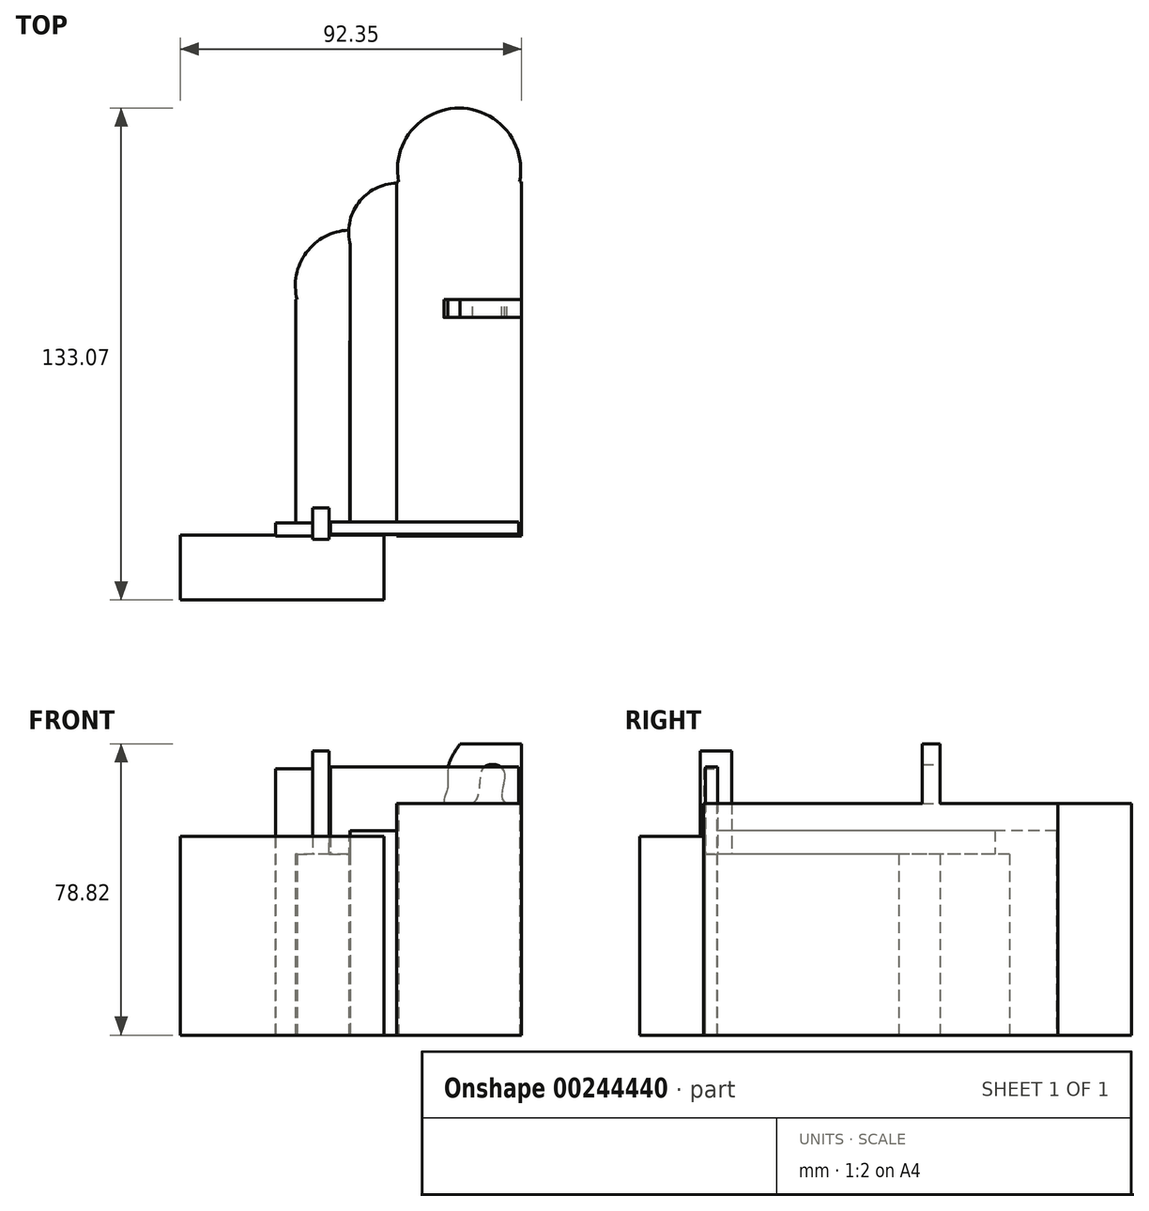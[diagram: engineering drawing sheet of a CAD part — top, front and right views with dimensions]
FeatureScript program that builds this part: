
annotation { "Feature Type Name" : "Feature", "Feature Type Description" : "" }
export const myFeature = defineFeature(function(context is Context, id is Id, definition is map)
    precondition{}
    {
        {
            var Q0;
            Q0=qCreatedBy(makeId("Top.planeOp"),FACE);
            var sketch = newSketch(context, id + "F0", { "sketchPlane" : qUnion([Q0])});
            skCircle(sketch, "E0", {"center": v(9.04, 35.12) * mm, "radius": 16.7 * mm});
            skSolve(sketch);
        }
        {
            var Q0;
            Q0 = qSketchRegion(id + "F0", true);
            extrude(context, id + "F1", {"entities" : qUnion([Q0]), "depth" : 62.74 * mm});
        }
        {
            var Q0;
            Q0=qCreatedBy(makeId("Top.planeOp"),FACE);
            var sketch = newSketch(context, id + "F2", { "sketchPlane" : qUnion([Q0])});
            skLineSegment(sketch, "E1.bottom", {"start": v(25.94, 31.92) * mm, "end": v(-7.87, 31.92) * mm});
            skLineSegment(sketch, "E1.top", {"start": v(25.94, -63.98) * mm, "end": v(-7.87, -63.98) * mm});
            skLineSegment(sketch, "E1.left", {"start": v(25.94, 31.92) * mm, "end": v(25.94, -63.98) * mm});
            skLineSegment(sketch, "E1.right", {"start": v(-7.87, 31.92) * mm, "end": v(-7.87, -63.98) * mm});
            skSolve(sketch);
        }
        {
            var Q0;
            Q0 = qSketchRegion(id + "F2", true);
            extrude(context, id + "F3", {"entities" : qUnion([Q0]), "operationType" : NewBodyOperationType.ADD, "depth" : 62.74 * mm});
        }
        {
            var Q0;
            Q0=qCreatedBy(makeId("Top.planeOp"),FACE);
            var sketch = newSketch(context, id + "F4", { "sketchPlane" : qUnion([Q0])});
            skCircle(sketch, "E2", {"center": v(-7.58, 18.24) * mm, "radius": 13.27 * mm});
            skSolve(sketch);
        }
        {
            var Q0;
            Q0 = qSketchRegion(id + "F4", true);
            extrude(context, id + "F5", {"entities" : qUnion([Q0]), "operationType" : NewBodyOperationType.ADD, "depth" : 55.37 * mm});
        }
        {
            var Q0;
            Q0=qCreatedBy(makeId("Top.planeOp"),FACE);
            var sketch = newSketch(context, id + "F6", { "sketchPlane" : qUnion([Q0])});
            skLineSegment(sketch, "E3.bottom", {"start": v(-7.87, 19.11) * mm, "end": v(-20.4, 19.11) * mm});
            skLineSegment(sketch, "E3.top", {"start": v(-7.87, -63.67) * mm, "end": v(-20.4, -63.67) * mm});
            skLineSegment(sketch, "E3.left", {"start": v(-7.87, 19.11) * mm, "end": v(-7.87, -63.67) * mm});
            skLineSegment(sketch, "E3.right", {"start": v(-20.4, 19.11) * mm, "end": v(-20.4, -63.67) * mm});
            skSolve(sketch);
        }
        {
            var Q0;
            Q0 = qSketchRegion(id + "F6", true);
            extrude(context, id + "F7", {"entities" : qUnion([Q0]), "operationType" : NewBodyOperationType.ADD, "depth" : 55.37 * mm});
        }
        {
            var Q0;
            Q0=qCreatedBy(makeId("Top.planeOp"),FACE);
            var sketch = newSketch(context, id + "F8", { "sketchPlane" : qUnion([Q0])});
            skCircle(sketch, "E4", {"center": v(-20.28, 3.79) * mm, "radius": 15 * mm});
            skSolve(sketch);
        }
        {
            var Q0;
            Q0 = qSketchRegion(id + "F8", true);
            extrude(context, id + "F9", {"entities" : qUnion([Q0]), "operationType" : NewBodyOperationType.ADD, "depth" : 49.02 * mm});
        }
        {
            var Q0;
            Q0=qCreatedBy(makeId("Top.planeOp"),FACE);
            var sketch = newSketch(context, id + "F10", { "sketchPlane" : qUnion([Q0])});
            skLineSegment(sketch, "E5.bottom", {"start": v(-20.57, 0) * mm, "end": v(-35.14, 0) * mm});
            skLineSegment(sketch, "E5.top", {"start": v(-20.57, -64.12) * mm, "end": v(-35.14, -64.12) * mm});
            skLineSegment(sketch, "E5.left", {"start": v(-20.57, 0) * mm, "end": v(-20.57, -64.12) * mm});
            skLineSegment(sketch, "E5.right", {"start": v(-35.14, 0) * mm, "end": v(-35.14, -64.12) * mm});
            skSolve(sketch);
        }
        {
            var Q0;
            Q0 = qSketchRegion(id + "F10", true);
            extrude(context, id + "F11", {"entities" : qUnion([Q0]), "operationType" : NewBodyOperationType.ADD, "depth" : 49.02 * mm});
        }
        {
            var Q0;
            Q0=qCreatedBy(makeId("Front.planeOp"),FACE);
            var sketch = newSketch(context, id + "F12", { "sketchPlane" : qUnion([Q0])});
            skLineSegment(sketch, "E6", {"start": v(25.94, 62.2) * mm, "end": v(25.94, 78.82) * mm});
            skLineSegment(sketch, "E7", {"start": v(25.94, 78.82) * mm, "end": v(9.33, 78.82) * mm});
            skFitSpline(sketch, "E8", {"points": [v(9.33, 78.82) * mm, v(6.12, 72.7) * mm, v(5.83, 66.58) * mm, v(5.25, 62.5) * mm, v(13.4, 63.38) * mm, v(15.74, 72.41) * mm, v(20.99, 71.83) * mm, v(20.7, 63.96) * mm, v(25.94, 62.2) * mm], "startDerivative": vector(-32.98, -46.7) * mm, "endDerivative": vector(61.94, -2.33) * mm});
            skSolve(sketch);
        }
        {
            var Q0;
            Q0 = qSketchRegion(id + "F12", true);
            extrude(context, id + "F13", {"entities" : qUnion([Q0]), "operationType" : NewBodyOperationType.ADD, "depth" : 4.83 * mm});
        }
        {
            var Q0;
            Q0=qCreatedBy(makeId("Top.planeOp"),FACE);
            var sketch = newSketch(context, id + "F14", { "sketchPlane" : qUnion([Q0])});
            skLineSegment(sketch, "E9.bottom", {"start": v(-30.54, -64.94) * mm, "end": v(-26.1, -64.94) * mm});
            skLineSegment(sketch, "E9.top", {"start": v(-30.54, -56.34) * mm, "end": v(-26.1, -56.34) * mm});
            skLineSegment(sketch, "E9.left", {"start": v(-30.54, -64.94) * mm, "end": v(-30.54, -56.34) * mm});
            skLineSegment(sketch, "E9.right", {"start": v(-26.1, -64.94) * mm, "end": v(-26.1, -56.34) * mm});
            skSolve(sketch);
        }
        {
            var Q0;
            Q0 = qSketchRegion(id + "F14", true);
            extrude(context, id + "F15", {"entities" : qUnion([Q0]), "operationType" : NewBodyOperationType.ADD, "depth" : 76.96 * mm});
        }
        {
            var Q0;
            Q0=qCreatedBy(makeId("Top.planeOp"),FACE);
            var sketch = newSketch(context, id + "F16", { "sketchPlane" : qUnion([Q0])});
            skLineSegment(sketch, "E10.bottom", {"start": v(-25.8, -60.2) * mm, "end": v(25.2, -60.2) * mm});
            skLineSegment(sketch, "E10.top", {"start": v(-25.8, -63.46) * mm, "end": v(25.2, -63.46) * mm});
            skLineSegment(sketch, "E10.left", {"start": v(-25.8, -60.2) * mm, "end": v(-25.8, -63.46) * mm});
            skLineSegment(sketch, "E10.right", {"start": v(25.2, -60.2) * mm, "end": v(25.2, -63.46) * mm});
            skSolve(sketch);
        }
        {
            var Q0;
            Q0 = qSketchRegion(id + "F16", true);
            extrude(context, id + "F17", {"entities" : qUnion([Q0]), "operationType" : NewBodyOperationType.ADD, "depth" : 72.64 * mm});
        }
        {
            var Q0;
            Q0=qCreatedBy(makeId("Top.planeOp"),FACE);
            var sketch = newSketch(context, id + "F18", { "sketchPlane" : qUnion([Q0])});
            skLineSegment(sketch, "E11.bottom", {"start": v(-30.54, -64.05) * mm, "end": v(-40.62, -64.05) * mm});
            skLineSegment(sketch, "E11.top", {"start": v(-30.54, -60.5) * mm, "end": v(-40.62, -60.5) * mm});
            skLineSegment(sketch, "E11.left", {"start": v(-30.54, -64.05) * mm, "end": v(-30.54, -60.5) * mm});
            skLineSegment(sketch, "E11.right", {"start": v(-40.62, -64.05) * mm, "end": v(-40.62, -60.5) * mm});
            skSolve(sketch);
        }
        {
            var Q0;
            Q0 = qSketchRegion(id + "F18", true);
            extrude(context, id + "F19", {"entities" : qUnion([Q0]), "operationType" : NewBodyOperationType.ADD, "depth" : 72.14 * mm});
        }
        {
            var Q0;
            Q0=qCreatedBy(makeId("Top.planeOp"),FACE);
            var sketch = newSketch(context, id + "F20", { "sketchPlane" : qUnion([Q0])});
            skLineSegment(sketch, "E12.bottom", {"start": v(-11.27, -63.76) * mm, "end": v(-66.41, -63.76) * mm});
            skLineSegment(sketch, "E12.top", {"start": v(-11.27, -81.25) * mm, "end": v(-66.41, -81.25) * mm});
            skLineSegment(sketch, "E12.left", {"start": v(-11.27, -63.76) * mm, "end": v(-11.27, -81.25) * mm});
            skLineSegment(sketch, "E12.right", {"start": v(-66.41, -63.76) * mm, "end": v(-66.41, -81.25) * mm});
            skSolve(sketch);
        }
        {
            var Q0;
            Q0 = qSketchRegion(id + "F20", true);
            extrude(context, id + "F21", {"entities" : qUnion([Q0]), "operationType" : NewBodyOperationType.ADD, "depth" : 53.85 * mm});
        }
    });
